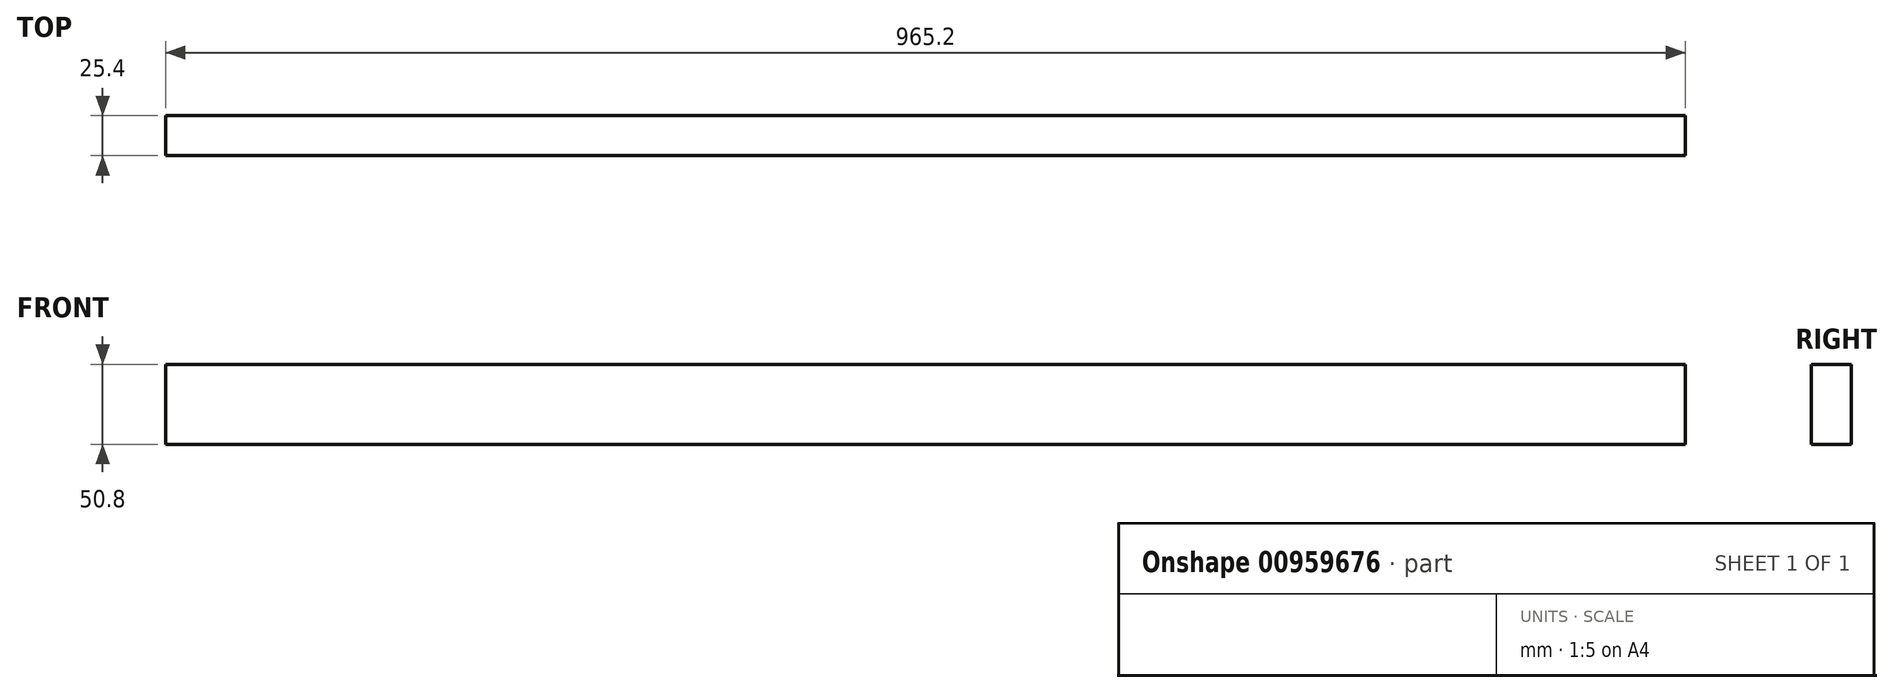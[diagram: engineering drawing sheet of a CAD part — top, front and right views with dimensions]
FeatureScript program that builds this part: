
annotation { "Feature Type Name" : "Feature", "Feature Type Description" : "" }
export const myFeature = defineFeature(function(context is Context, id is Id, definition is map)
    precondition{}
    {
        {
            var Q0;
            Q0=qCreatedBy(makeId("Top.planeOp"),FACE);
            var sketch = newSketch(context, id + "F0", { "sketchPlane" : qUnion([Q0])});
            skLineSegment(sketch, "E0.bottom", {"start": v(-62, 9.07) * mm, "end": v(903.2, 9.07) * mm});
            skLineSegment(sketch, "E0.top", {"start": v(-62, -16.33) * mm, "end": v(903.2, -16.33) * mm});
            skLineSegment(sketch, "E0.left", {"start": v(-62, 9.07) * mm, "end": v(-62, -16.33) * mm});
            skLineSegment(sketch, "E0.right", {"start": v(903.2, 9.07) * mm, "end": v(903.2, -16.33) * mm});
            skSolve(sketch);
        }
        {
            var Q0;
            Q0=makeQuery(id+"F0.imprint","IMPRINT",FACE,{"disambiguationData":[TD([[makeQuery(id+"F0.imprint","IMPRINT",EDGE,{"derivedFrom":sQuery(id+"F0.wireOp",EDGE,"E0.bottom")}),-1.0]])]});
            extrude(context, id + "F1", {"entities" : qUnion([Q0]), "depth" : 50.8 * mm, "offsetDistance" : 25.4 * mm});
        }
    });
